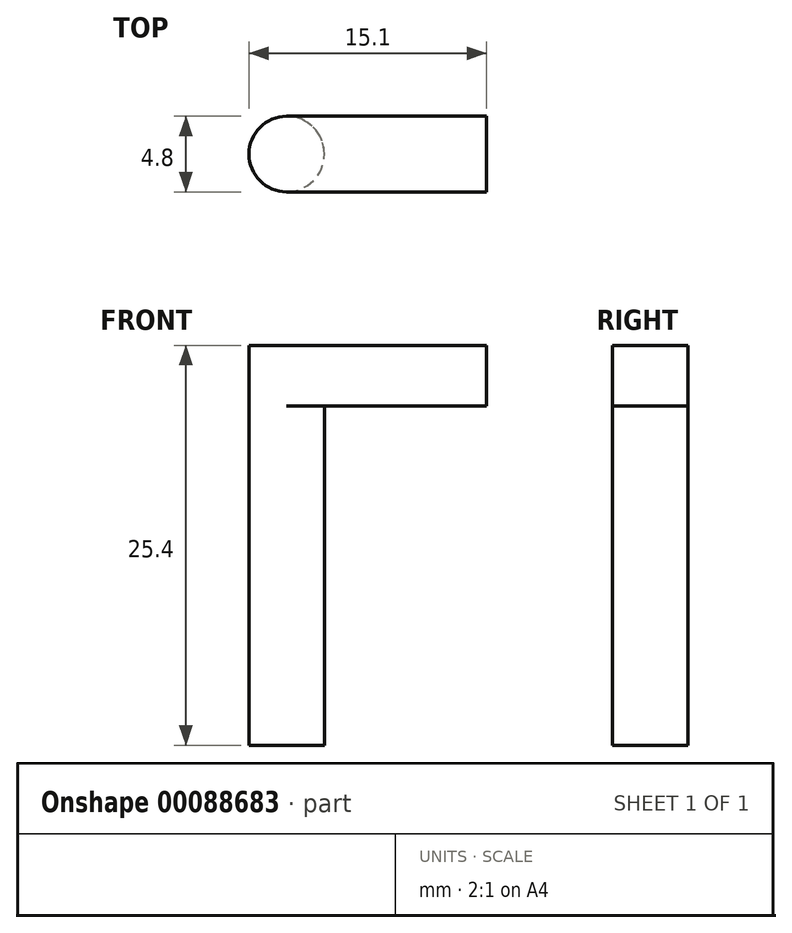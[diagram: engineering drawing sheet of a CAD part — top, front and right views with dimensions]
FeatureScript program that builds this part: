
annotation { "Feature Type Name" : "Feature", "Feature Type Description" : "" }
export const myFeature = defineFeature(function(context is Context, id is Id, definition is map)
    precondition{}
    {
        {
            var Q0;
            Q0=qCreatedBy(makeId("Top.planeOp"),FACE);
            var sketch = newSketch(context, id + "F0", { "sketchPlane" : qUnion([Q0])});
            skCircle(sketch, "E0", {"center": v(0, 0) * mm, "radius": 2.4 * mm});
            skSolve(sketch);
        }
        {
            var Q0;
            Q0=makeQuery(id+"F0.imprint","IMPRINT",FACE,{"disambiguationData":[TD([[makeQuery(id+"F0.imprint","IMPRINT",EDGE,{"derivedFrom":sQuery(id+"F0.wireOp",EDGE,"E0")}),1.0]])]});
            extrude(context, id + "F1", {"entities" : qUnion([Q0]), "depth" : 25.4 * mm});
        }
        {
            var Q0;
            Q0=qCreatedBy(makeId("Right.planeOp"),FACE);
            var sketch = newSketch(context, id + "F2", { "sketchPlane" : qUnion([Q0])});
            skLineSegment(sketch, "E1.0", {"start": v(-2.4, 25.4) * mm, "end": v(2.4, 25.4) * mm, "construction": true});
            skLineSegment(sketch, "E2.bottom", {"start": v(-2.4, 25.4) * mm, "end": v(2.4, 25.4) * mm});
            skLineSegment(sketch, "E2.top", {"start": v(-2.4, 21.56) * mm, "end": v(2.4, 21.56) * mm});
            skLineSegment(sketch, "E2.left", {"start": v(-2.4, 25.4) * mm, "end": v(-2.4, 21.56) * mm});
            skLineSegment(sketch, "E2.right", {"start": v(2.4, 25.4) * mm, "end": v(2.4, 21.56) * mm});
            skSolve(sketch);
        }
        {
            var Q0;
            Q0 = qSketchRegion(id + "F2", true);
            extrude(context, id + "F3", {"entities" : qUnion([Q0]), "operationType" : NewBodyOperationType.ADD, "depth" : 12.7 * mm});
        }
    });
